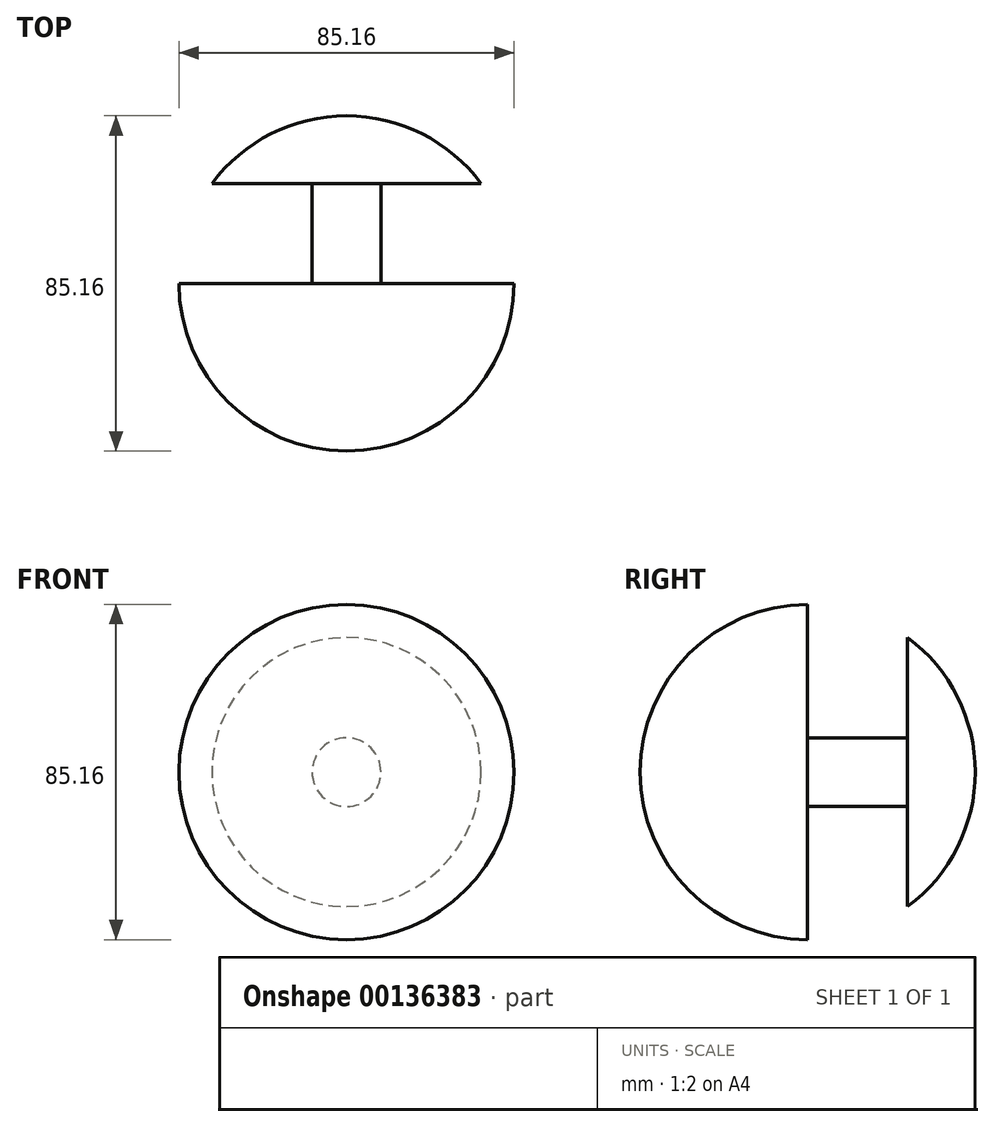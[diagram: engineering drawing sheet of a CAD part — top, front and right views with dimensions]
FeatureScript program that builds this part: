
annotation { "Feature Type Name" : "Feature", "Feature Type Description" : "" }
export const myFeature = defineFeature(function(context is Context, id is Id, definition is map)
    precondition{}
    {
        {
            var Q0;
            Q0=qCreatedBy(makeId("Front.planeOp"),FACE);
            var sketch = newSketch(context, id + "F0", { "sketchPlane" : qUnion([Q0])});
            skCircle(sketch, "E0", {"center": v(0, 0) * mm, "radius": 42.58 * mm});
            skLineSegment(sketch, "E1", {"start": v(0, 0) * mm, "end": v(0, 40.51) * mm});
            skLineSegment(sketch, "E2", {"start": v(0, 40.51) * mm, "end": v(0, 75.94) * mm});
            skLineSegment(sketch, "E3", {"start": v(0, 0) * mm, "end": v(0, -75.36) * mm});
            skCircle(sketch, "E4", {"center": v(0, 0) * mm, "radius": 8.74 * mm});
            skSolve(sketch);
        }
        {
            var Q0;
            {var subQ5=sQuery(id+"F0.wireOp",EDGE,"E1");Q0=makeQuery(id+"F0.imprint","IMPRINT",FACE,{"disambiguationData":[TD([[makeQuery(id+"F0.imprint","IMPRINT",EDGE,{"derivedFrom":subQ5}),1.0]])]});}
            var Q1;
            {var subQ1=sQuery(id+"F0.wireOp",EDGE,"E0");var subQ5=sQuery(id+"F0.wireOp",EDGE,"E2");var subQ8=makeQuery(id+"F0.imprint","INTERSECT",VERTEX,{"derivedFrom":[subQ1,subQ5]});Q1=makeQuery(id+"F0.imprint","IMPRINT",FACE,{"disambiguationData":[TD([[makeQuery(id+"F0.imprint","IMPRINT",EDGE,{"disambiguationData":[TD([[subQ8,-1.0]])],"derivedFrom":subQ1}),1.0]])]});}
            var Q2;
            Q2=sQuery(id+"F0.wireOp",EDGE,"E1");
            revolve(context, id + "F1", {"entities" : qUnion([Q0, Q1]), "axis" : qUnion([Q2]), "revolveType" : RevolveType.FULL});
        }
        {
            var Q0;
            Q0 = qSketchRegion(id + "F0", true);
            extrude(context, id + "F2", {"entities" : qUnion([Q0]), "operationType" : NewBodyOperationType.REMOVE, "oppositeDirection" : true, "depth" : 25.4 * mm});
        }
    });
